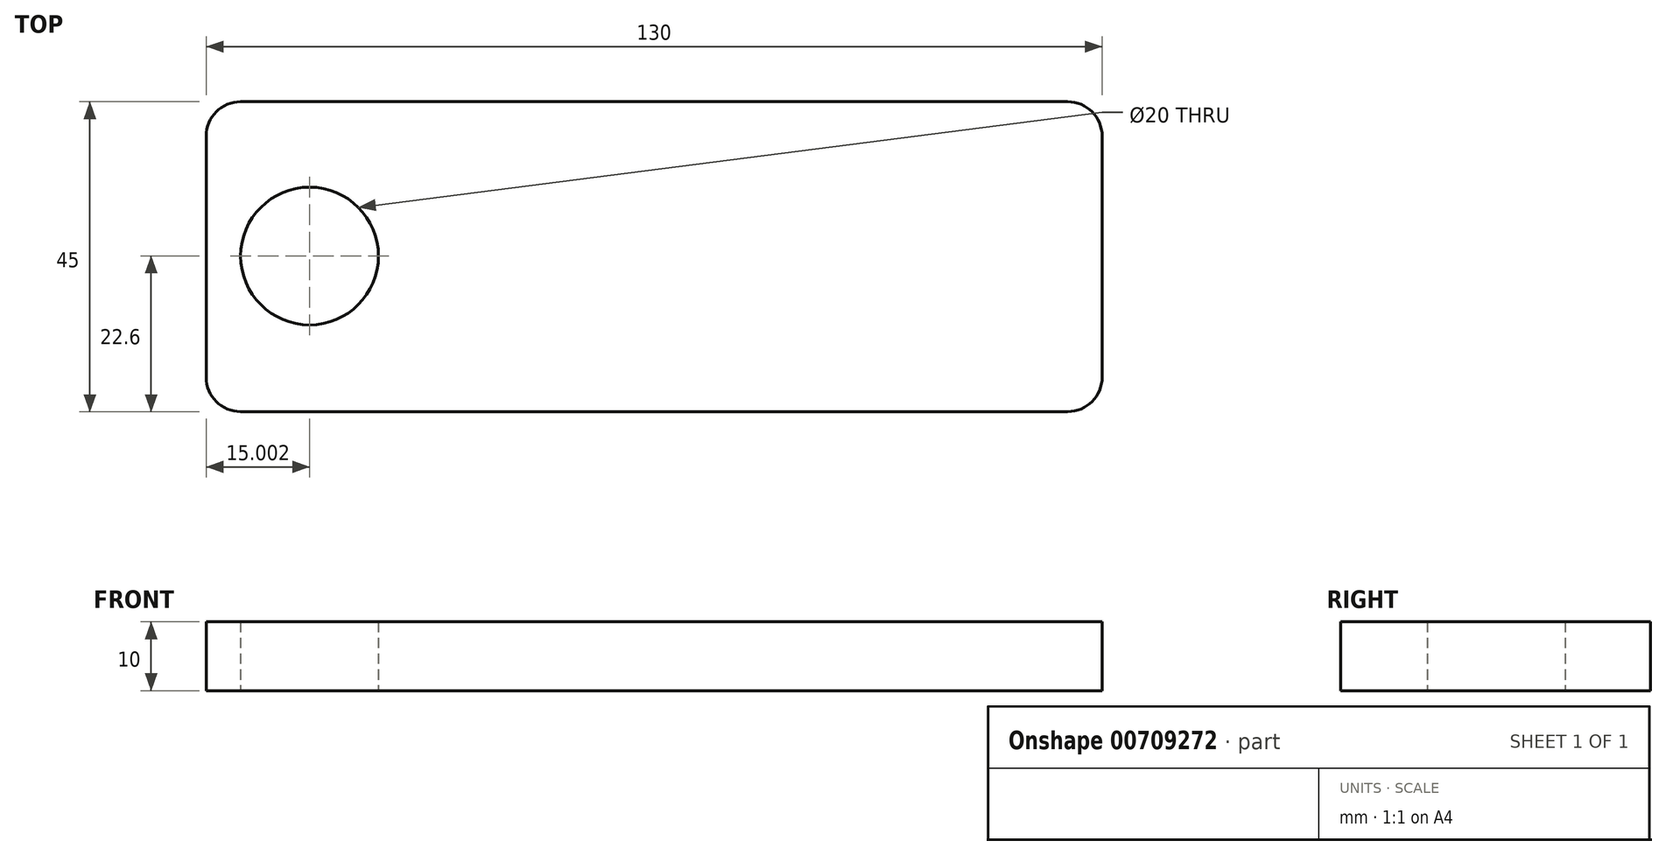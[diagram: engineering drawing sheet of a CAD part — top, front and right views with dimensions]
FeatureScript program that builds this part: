
annotation { "Feature Type Name" : "Feature", "Feature Type Description" : "" }
export const myFeature = defineFeature(function(context is Context, id is Id, definition is map)
    precondition{}
    {
        {
            var Q0;
            Q0=qCreatedBy(makeId("Top.planeOp"),FACE);
            var sketch = newSketch(context, id + "F0", { "sketchPlane" : qUnion([Q0])});
            skLineSegment(sketch, "E0.bottom", {"start": v(65, -22.6) * mm, "end": v(-65, -22.6) * mm});
            skLineSegment(sketch, "E0.top", {"start": v(65, 22.4) * mm, "end": v(-65, 22.4) * mm});
            skLineSegment(sketch, "E0.left", {"start": v(65, -22.6) * mm, "end": v(65, 22.4) * mm});
            skLineSegment(sketch, "E0.right", {"start": v(-65, -22.6) * mm, "end": v(-65, 22.4) * mm});
            skCircle(sketch, "E1", {"center": v(-50, 0) * mm, "radius": 10 * mm});
            skSolve(sketch);
        }
        {
            var Q0;
            Q0=makeQuery(id+"F0.imprint","IMPRINT",FACE,{"disambiguationData":[TD([[makeQuery(id+"F0.imprint","IMPRINT",EDGE,{"derivedFrom":sQuery(id+"F0.wireOp",EDGE,"E0.bottom")}),-1.0]])]});
            extrude(context, id + "F1", {"entities" : qUnion([Q0]), "depth" : 10 * mm, "offsetDistance" : 25 * mm});
        }
        {
            var Q0;
            Q0=makeQuery(id+"F1.opExtrude","SWEPT_EDGE",EDGE,{"disambiguationData":[OSD([sQuery(id+"F0.wireOp",EDGE,"E0.bottom"),sQuery(id+"F0.wireOp",EDGE,"E0.left")])]});
            var Q1;
            Q1=makeQuery(id+"F1.opExtrude","SWEPT_EDGE",EDGE,{"disambiguationData":[OSD([sQuery(id+"F0.wireOp",EDGE,"E0.top"),sQuery(id+"F0.wireOp",EDGE,"E0.left")])]});
            var Q2;
            Q2=makeQuery(id+"F1.opExtrude","SWEPT_EDGE",EDGE,{"disambiguationData":[OSD([sQuery(id+"F0.wireOp",EDGE,"E0.bottom"),sQuery(id+"F0.wireOp",EDGE,"E0.right")])]});
            var Q3;
            Q3=makeQuery(id+"F1.opExtrude","SWEPT_EDGE",EDGE,{"disambiguationData":[OSD([sQuery(id+"F0.wireOp",EDGE,"E0.top"),sQuery(id+"F0.wireOp",EDGE,"E0.right")])]});
            fillet(context, id + "F2", {"entities" : qUnion([Q0, Q1, Q2, Q3]), "radius" : 5 * mm, "tangentPropagation" : true, "allowEdgeOverflow" : false});
        }
    });
